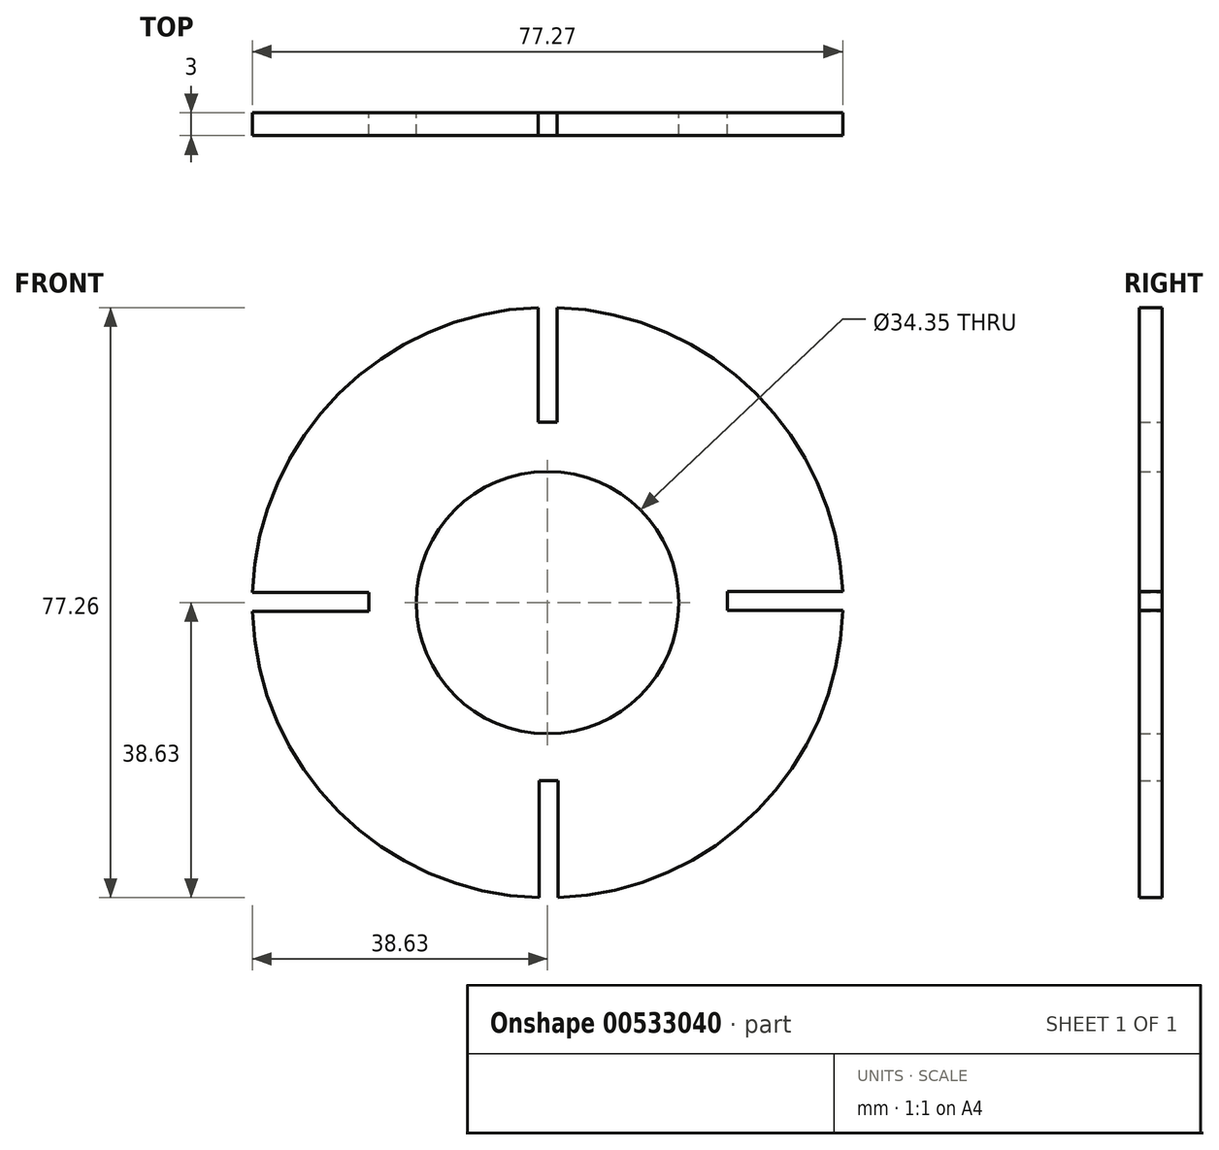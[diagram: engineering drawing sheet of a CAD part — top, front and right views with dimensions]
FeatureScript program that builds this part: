
annotation { "Feature Type Name" : "Feature", "Feature Type Description" : "" }
export const myFeature = defineFeature(function(context is Context, id is Id, definition is map)
    precondition{}
    {
        {
            var Q0;
            Q0=qCreatedBy(makeId("Front.planeOp"),FACE);
            var sketch = newSketch(context, id + "F0", { "sketchPlane" : qUnion([Q0])});
            skCircle(sketch, "E0", {"center": v(0, 0) * mm, "radius": 38.65 * mm});
            skLineSegment(sketch, "E1.bottom", {"start": v(1.25, 23.65) * mm, "end": v(-1.25, 23.65) * mm});
            skLineSegment(sketch, "E1.top", {"start": v(1.25, 53.65) * mm, "end": v(-1.25, 53.65) * mm});
            skLineSegment(sketch, "E1.left", {"start": v(1.25, 23.65) * mm, "end": v(1.25, 53.65) * mm});
            skLineSegment(sketch, "E1.right", {"start": v(-1.25, 23.65) * mm, "end": v(-1.25, 53.65) * mm});
            skPoint(sketch, "E1.middle", {"position": v(0, 38.65) * mm});
            skLineSegment(sketch, "E2.1.0", {"start": v(-53.42, 1.34) * mm, "end": v(-53.42, -1.16) * mm});
            skLineSegment(sketch, "E2.1.1", {"start": v(-23.42, 1.34) * mm, "end": v(-53.42, 1.34) * mm});
            skLineSegment(sketch, "E2.1.2", {"start": v(-23.42, -1.16) * mm, "end": v(-53.42, -1.16) * mm});
            skLineSegment(sketch, "E2.1.3", {"start": v(-23.42, 1.34) * mm, "end": v(-23.42, -1.16) * mm});
            skLineSegment(sketch, "E2.2.0", {"start": v(-1.1, -53.33) * mm, "end": v(1.4, -53.33) * mm});
            skLineSegment(sketch, "E2.2.1", {"start": v(-1.1, -23.33) * mm, "end": v(-1.1, -53.33) * mm});
            skLineSegment(sketch, "E2.2.2", {"start": v(1.4, -23.33) * mm, "end": v(1.4, -53.33) * mm});
            skLineSegment(sketch, "E2.2.3", {"start": v(-1.1, -23.33) * mm, "end": v(1.4, -23.33) * mm});
            skLineSegment(sketch, "E2.3.0", {"start": v(53.56, -1.02) * mm, "end": v(53.56, 1.48) * mm});
            skLineSegment(sketch, "E2.3.1", {"start": v(23.56, -1.02) * mm, "end": v(53.56, -1.02) * mm});
            skLineSegment(sketch, "E2.3.2", {"start": v(23.56, 1.48) * mm, "end": v(53.56, 1.48) * mm});
            skLineSegment(sketch, "E2.3.3", {"start": v(23.56, -1.02) * mm, "end": v(23.56, 1.48) * mm});
            skPoint(sketch, "E2.center", {"position": v(0.07, 0.16) * mm});
            skCircle(sketch, "E3", {"center": v(0, 0) * mm, "radius": 17.17 * mm});
            skSolve(sketch);
        }
        {
            var Q0;
            {var subQ5=sQuery(id+"F0.wireOp",EDGE,"E1.bottom");Q0=makeQuery(id+"F0.imprint","IMPRINT",FACE,{"disambiguationData":[TD([[makeQuery(id+"F0.imprint","IMPRINT",EDGE,{"derivedFrom":subQ5}),1.0]])]});}
            extrude(context, id + "F1", {"entities" : qUnion([Q0]), "depth" : 3 * mm, "offsetDistance" : 25 * mm});
        }
    });
